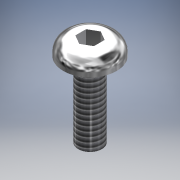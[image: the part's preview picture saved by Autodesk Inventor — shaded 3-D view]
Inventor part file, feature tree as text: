
AUTODESK INVENTOR PART (.ipt)
format: ipt  version: 2017 (Build 210142000, 142)  size: 132,608 bytes
history: native  units: in
note: dims shown in document units (in); Inventor stores cm internally (conversion verified against a paired STEP export)
features: extrude x2, sketch x2, fillet x1, thread x1
ambient origin geometry x8: Origin, YZ Plane, XZ Plane, XY Plane, X Axis, Y Axis, Z Axis, Center Point
bodies: Solid1 (feature_tree)
feature tree (6):
  extrude  "Extrusion1"  Depth=0.315in TaperAngle=0.0deg
  extrude  "Extrusion2"  Depth=0.05in
  fillet  "Fillet1"  Radius=0.05in
  thread  "Thread1"  [1 undecoded]
  sketch  "Sketch1"  dims[d0=0.099in d1=0.315in d2=0.0in]
  sketch  "Sketch2"  dims[d5=0.065in d6=0.0in d7=0.039in d8=0.05in d9=1.0in d10=0.0in]
note: 1 required parameter value undecoded (feature->parameter linkage not recoverable at this tier; creation-order binding heuristic only, values carry confidence <= 0.55)
